# Revit family: BIM_Model_Sanimat_4002_50_XFP_80C_CB1.1
name_source: partatom
category: Mechanical Equipment
revit_build: Autodesk Revit 2018 (Build: 20170223_1515(x64)
units: mm (PartAtom-declared; Revit-internal decimal feet)

## family parameters
Always vertical = Yes
Cut with Voids When Loaded = No
Part Type = Normal
Room Calculation Point = No
Round Connector Dimension = Use Radius
Shared = No
Work Plane-Based = No

## types (6) — shared parameters
Bottom Plate = Cast Iron EN-GJL-250
Description = Flood-proof double lifting station for automatic sewage pumping from areas below the backwash level in accordance with EN 12050-1.
Discharge Connection = Sleeve 4'' DN 100
Discharge Flange DN 80 = 40 mm  [stored 0.131234 ft]
Impeller = Cast Iron EN-GJL-250
Inflow DN 100 = 50 mm  [stored 0.164042 ft]
Inflow DN 100/150 = 50 mm  [stored 0.164042 ft]
Inflow DN 150/200 = 75 mm  [stored 0.246063 ft]
Inflow/Hand Membrane Pump DN 40 = 20 mm  [stored 0.0656168 ft]
Manufacturer = Sulzer
Model = Lifting Station Type ABS Sanimat 4002
Motor Housing = Cast Iron EN-GJL-250
Product Specification Link = http://www.sulzer.com
Pump Connection DN 100 = 50 mm  [stored 0.164042 ft]
Rated Voltage (V) = 400 3~
Rotor shatf = Stainless steel 1.4021 (AISI 420)
Solids Size = 75
Tank Material = Polyethylene
Vent/Inflow DN 70 = 35 mm  [stored 0.114829 ft]
Volute = Cast Iron EN-GJL-250

## per-type parameters (varying)
| type | Cable Length (m) | Cable Type / Starting | Motor | Motor Power (kW) | Pump Discharge DN | Rated Current (A) | Speed (r/min) | Weight (Kg) |
| 80C-CB1.1 |  | (a) / DOL | PE13/6C | P1=1.6 P2=1.3 | 80 mm  [stored 0.262467 ft] | 3.6 | 980 | 231 |
| 80C-CB1.3 | 10m | (a) / DOL | PE22/4C | P1=2.5 P2=2.2 | 80 mm  [stored 0.262467 ft] | 4.6 | 1450 | 231 |
| 100C-CB1.3 |  | (a) / DOL | PE22/4C | P1=2.5 P2=2.2 | 100 mm  [stored 0.328084 ft] | 4.6 | 1450 | 245 |
| 100C-CB1.2 |  | (a) / DOL | PE29/4C | P1=3.4 P2=3.0 | 100 mm  [stored 0.328084 ft] | 6.4 | 1450 | 249 |
| 100E-CB1.3 |  | (b) / YΔ | PE60/4C | P1=6.7 P2=6.0 | 100 mm  [stored 0.328084 ft] | 13.6 | 1450 | 387 |
| 100E-CB1.4 |  | (b) / YΔ | PE60/4C | P1=6.7 P2=6.0 | 100 mm  [stored 0.328084 ft] | 13.6 | 1450 | 387 |

note: [stored X ft] marks values corroborated as IEEE doubles in the binary element streams (Revit-internal decimal feet)

## geometry (parser evidence)
native form markers: Sweep x2
no freeform markers — native parametric forms only
